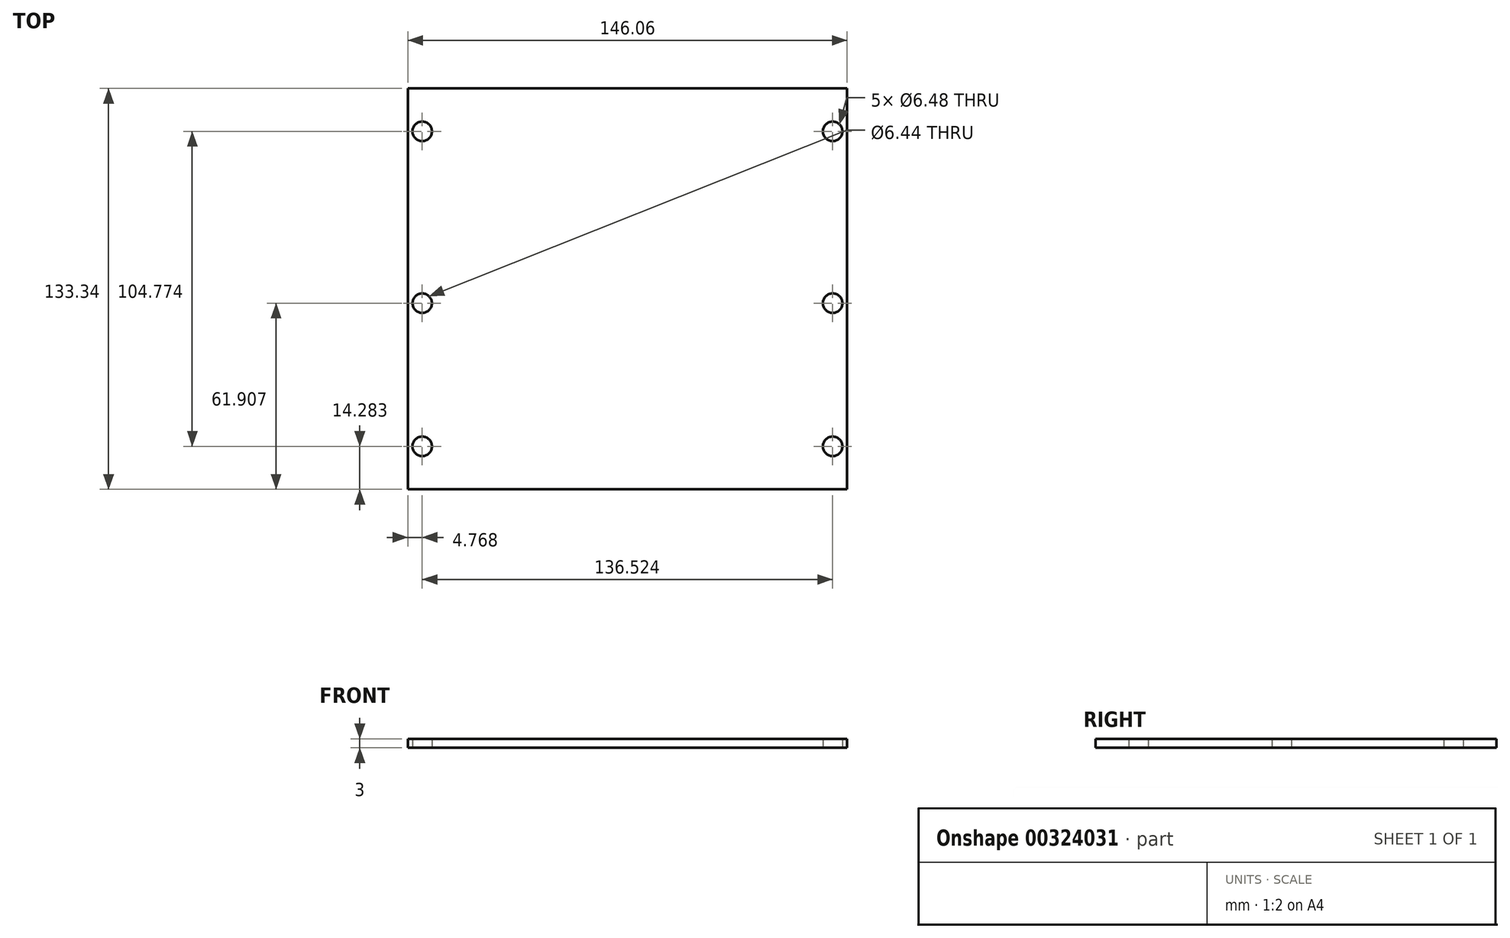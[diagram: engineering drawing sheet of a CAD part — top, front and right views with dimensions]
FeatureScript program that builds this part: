
annotation { "Feature Type Name" : "Feature", "Feature Type Description" : "" }
export const myFeature = defineFeature(function(context is Context, id is Id, definition is map)
    precondition{}
    {
        {
            var Q0;
            Q0=qCreatedBy(makeId("Top.planeOp"),FACE);
            var sketch = newSketch(context, id + "F0", { "sketchPlane" : qUnion([Q0])});
            skLineSegment(sketch, "E0", {"start": v(72.22, 1.59) * mm, "end": v(72.22, 46.04) * mm});
            skLineSegment(sketch, "E1", {"start": v(68.26, 46.04) * mm, "end": v(72.22, 46.04) * mm});
            skArc(sketch, "E2", {"start": v(68.26, 1.59) * mm, "mid": v(61.91, -4.76) * mm, "end": v(68.26, -11.11) * mm});
            skLineSegment(sketch, "E3", {"start": v(68.26, 1.59) * mm, "end": v(72.22, 1.59) * mm});
            skArc(sketch, "E4", {"start": v(68.26, -46.04) * mm, "mid": v(61.91, -52.39) * mm, "end": v(68.26, -58.74) * mm});
            skLineSegment(sketch, "E5", {"start": v(68.26, -11.11) * mm, "end": v(72.22, -11.11) * mm});
            skLineSegment(sketch, "E6", {"start": v(72.22, -46.04) * mm, "end": v(72.22, -11.11) * mm});
            skLineSegment(sketch, "E7", {"start": v(68.26, -46.04) * mm, "end": v(72.22, -46.04) * mm});
            skLineSegment(sketch, "E8", {"start": v(-72.23, -65.88) * mm, "end": v(-72.23, -58.74) * mm});
            skLineSegment(sketch, "E9", {"start": v(-68.26, -58.74) * mm, "end": v(-72.23, -58.74) * mm});
            skArc(sketch, "E10", {"start": v(-68.26, -58.74) * mm, "mid": v(-61.91, -52.39) * mm, "end": v(-68.26, -46.04) * mm});
            skLineSegment(sketch, "E11", {"start": v(72.22, -65.88) * mm, "end": v(72.22, -58.74) * mm});
            skLineSegment(sketch, "E12", {"start": v(68.26, -58.74) * mm, "end": v(72.22, -58.74) * mm});
            skLineSegment(sketch, "E13", {"start": v(72.22, -65.88) * mm, "end": v(-72.23, -65.88) * mm});
            skLineSegment(sketch, "E14", {"start": v(-68.26, -11.2) * mm, "end": v(-72.23, -11.2) * mm});
            skArc(sketch, "E15", {"start": v(-67.1, -10.98) * mm, "mid": v(-67.67, -11.15) * mm, "end": v(-68.26, -11.2) * mm});
            skArc(sketch, "E16", {"start": v(-67.1, -11) * mm, "mid": v(-61.94, -4.18) * mm, "end": v(-68.26, 1.59) * mm});
            skLineSegment(sketch, "E17", {"start": v(-72.23, -46.04) * mm, "end": v(-72.23, -11.2) * mm});
            skLineSegment(sketch, "E18", {"start": v(-68.26, -46.04) * mm, "end": v(-72.23, -46.04) * mm});
            skLineSegment(sketch, "E19", {"start": v(-68.26, 1.59) * mm, "end": v(-72.23, 1.59) * mm});
            skLineSegment(sketch, "E20", {"start": v(-68.26, 46.04) * mm, "end": v(-72.23, 46.04) * mm});
            skLineSegment(sketch, "E21", {"start": v(-72.23, 1.59) * mm, "end": v(-72.23, 46.04) * mm});
            skLineSegment(sketch, "E22", {"start": v(-68.26, 58.74) * mm, "end": v(-72.23, 58.74) * mm});
            skLineSegment(sketch, "E23", {"start": v(-72.23, 58.74) * mm, "end": v(-72.23, 65.88) * mm});
            skLineSegment(sketch, "E24", {"start": v(-72.23, 65.88) * mm, "end": v(72.23, 65.88) * mm});
            skArc(sketch, "E25", {"start": v(-68.26, 46.04) * mm, "mid": v(-61.91, 52.39) * mm, "end": v(-68.26, 58.74) * mm});
            skLineSegment(sketch, "E26", {"start": v(72.22, 58.74) * mm, "end": v(72.22, 65.88) * mm});
            skLineSegment(sketch, "E27", {"start": v(68.26, 58.74) * mm, "end": v(72.22, 58.74) * mm});
            skArc(sketch, "E28", {"start": v(68.26, 58.74) * mm, "mid": v(61.91, 52.39) * mm, "end": v(68.26, 46.04) * mm});
            skArc(sketch, "E29", {"start": v(-68.26, -11.2) * mm, "mid": v(-68.86, -11.15) * mm, "end": v(-69.43, -10.98) * mm});
            skCircle(sketch, "E30", {"center": v(68.26, 52.39) * mm, "radius": 3.24 * mm});
            skCircle(sketch, "E31", {"center": v(-68.26, -52.39) * mm, "radius": 3.24 * mm});
            skCircle(sketch, "E32", {"center": v(68.26, -52.39) * mm, "radius": 3.24 * mm});
            skCircle(sketch, "E33", {"center": v(68.26, -4.76) * mm, "radius": 3.24 * mm});
            skCircle(sketch, "E34", {"center": v(-68.26, -4.76) * mm, "radius": 3.22 * mm});
            skLineSegment(sketch, "E35", {"start": v(-73.03, 66.67) * mm, "end": v(73.03, 66.67) * mm});
            skLineSegment(sketch, "E36", {"start": v(73.03, -66.67) * mm, "end": v(73.03, 66.67) * mm});
            skLineSegment(sketch, "E37", {"start": v(73.03, -66.67) * mm, "end": v(-73.03, -66.67) * mm});
            skLineSegment(sketch, "E38", {"start": v(-73.03, -66.67) * mm, "end": v(-73.03, 66.67) * mm});
            skCircle(sketch, "E39", {"center": v(-68.26, 52.39) * mm, "radius": 3.24 * mm});
            skSolve(sketch);
        }
        {
            var Q0;
            Q0 = qSketchRegion(id + "F0", true);
            extrude(context, id + "F1", {"entities" : qUnion([Q0]), "depth" : 3 * mm});
        }
    });
